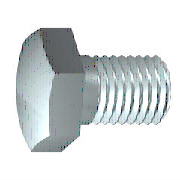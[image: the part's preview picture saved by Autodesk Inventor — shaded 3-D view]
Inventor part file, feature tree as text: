
AUTODESK INVENTOR PART (.ipt)
format: ipt  version: 2023 (Build 270158000, 158)  size: 189,952 bytes
history: native  units: mm (DEFAULTED — no unit token found)
features: other x2, sketch x2, extrude x1, fillet x1, plane x1
ambient origin geometry x7: Origin, YZ Plane, XZ Plane, X Axis, Y Axis, Z Axis, Center Point
bodies: Solid1 (feature_tree)
feature tree (7):
  other  "Базовый элемент"
  extrude  "С головкой"  Depth=10.0mm
  other  "Фаска1"
  fillet  "Fillet"  [1 undecoded]
  plane  "Work Plane1"
  sketch  "Эскиз1"
  sketch  "Эскиз2"
note: 1 required parameter value undecoded (feature->parameter linkage not recoverable at this tier; creation-order binding heuristic only, values carry confidence <= 0.55)
